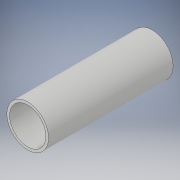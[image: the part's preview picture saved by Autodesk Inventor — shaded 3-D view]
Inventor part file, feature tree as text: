
AUTODESK INVENTOR PART (.ipt)
format: ipt  version: 2019 (Build 230136000, 136)  size: 101,888 bytes
history: native  units: mm
features: extrude x2, sketch x2
ambient origin geometry x8: Origin, YZ Plane, XZ Plane, XY Plane, X Axis, Y Axis, Z Axis, Center Point
bodies: Solid1 (feature_tree)
feature tree (4):
  extrude  "Extrusion1"  Depth=1200.0mm TaperAngle=0.0deg
  extrude  "Extrusion2"  Depth=120.0mm TaperAngle=0.0deg
  sketch  "Sketch1"  dims[d0=402.0mm d1=1200.0mm d2=0.0mm]
  sketch  "Sketch2"  dims[d3=350.0mm d4=120.0mm d5=0.0mm]
